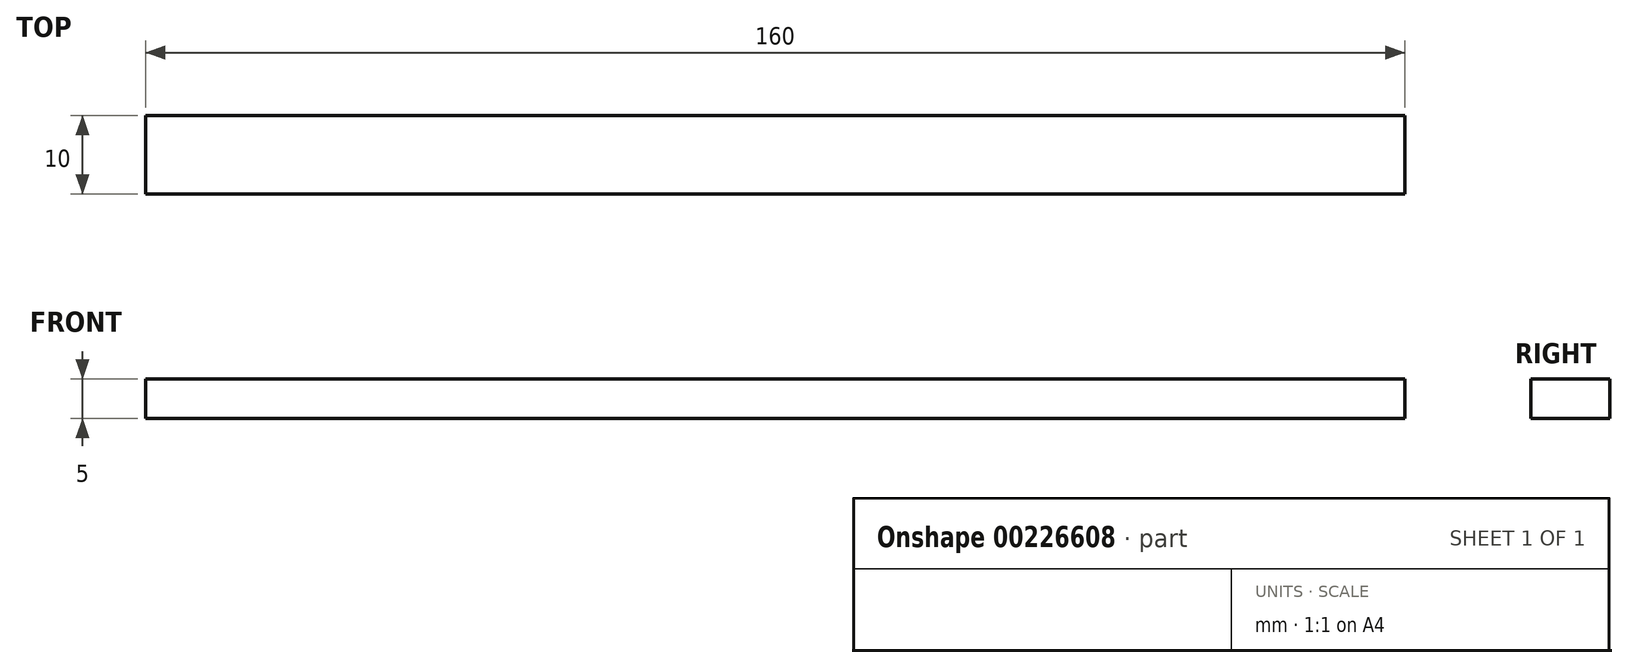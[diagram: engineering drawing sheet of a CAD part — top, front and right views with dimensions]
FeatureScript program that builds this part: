
annotation { "Feature Type Name" : "Feature", "Feature Type Description" : "" }
export const myFeature = defineFeature(function(context is Context, id is Id, definition is map)
    precondition{}
    {
        {
            var Q0;
            Q0=qCreatedBy(makeId("Top.planeOp"),FACE);
            var sketch = newSketch(context, id + "F0", { "sketchPlane" : qUnion([Q0])});
            skLineSegment(sketch, "E0.bottom", {"start": v(-80, 5) * mm, "end": v(80, 5) * mm});
            skLineSegment(sketch, "E0.top", {"start": v(-80, -5) * mm, "end": v(80, -5) * mm});
            skLineSegment(sketch, "E0.left", {"start": v(-80, 5) * mm, "end": v(-80, -5) * mm});
            skLineSegment(sketch, "E0.right", {"start": v(80, 5) * mm, "end": v(80, -5) * mm});
            skLineSegment(sketch, "E1", {"start": v(-80, -5) * mm, "end": v(80, 5) * mm, "construction": true});
            skLineSegment(sketch, "E2", {"start": v(-80, 5) * mm, "end": v(80, -5) * mm, "construction": true});
            skSolve(sketch);
        }
        {
            var Q0;
            Q0=qSketchRegion(id+"F0",true);
            extrude(context, id + "F1", {"entities" : qUnion([Q0]), "depth" : 5 * mm});
        }
    });
